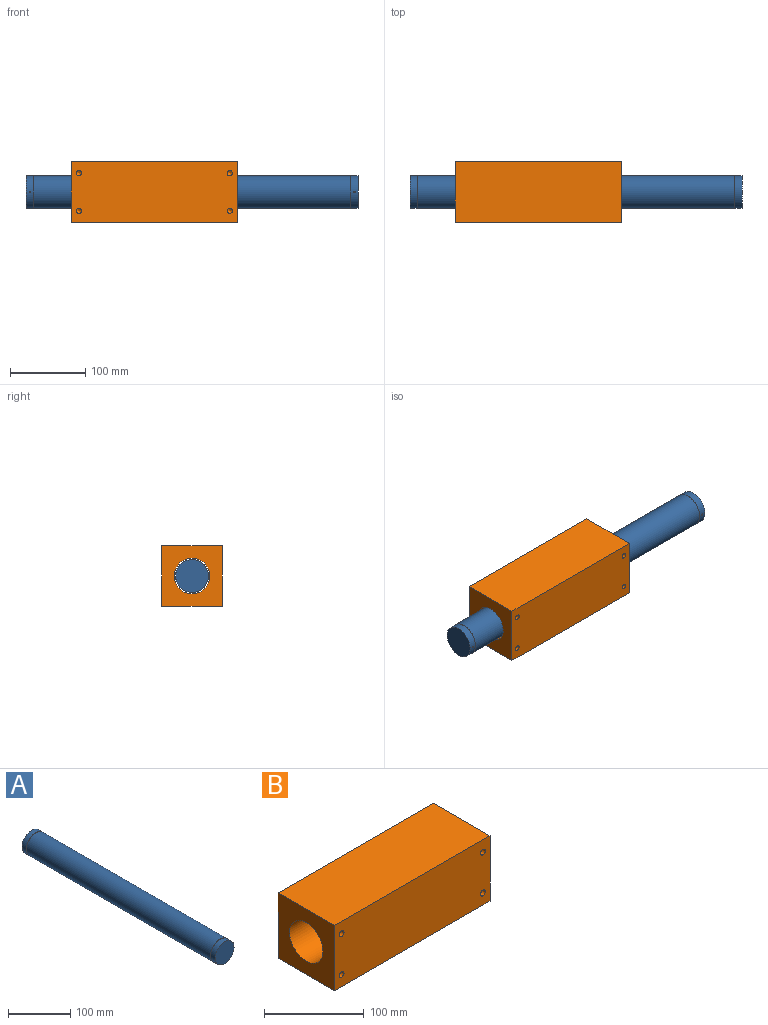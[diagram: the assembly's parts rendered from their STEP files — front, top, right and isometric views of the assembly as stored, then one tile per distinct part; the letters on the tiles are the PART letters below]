
ASSEMBLY  parts=2 mates=1
PART A: 11 faces, bbox 43.5x440x43.5 mm
  f0: cylinder r=21.65mm len=43.3mm, axis (0,1,0), area 1355.4mm2, adj f3,f4,f10
  f1: cylinder r=21.65mm len=43.3mm, axis (0,1,0), area 1355.4mm2, adj f5,f6,f8
  f2: cylinder r=21.75mm len=420mm, axis (0,1,0), area 57396.9mm2, adj f3,f5
  f3: plane 43.5x43.5mm, normal (0,1,0), area 13.6mm2, adj f0,f2
  f4: plane 43.3x43.3mm, normal (0,1,0), area 1472.5mm2, adj f0
  f5: plane 43.5x43.5mm, normal (0,-1,0), area 13.6mm2, adj f1,f2
  f6: plane 43.3x43.3mm, normal (0,-1,0), area 1472.5mm2, adj f1
  f7: plane 2.5x2.5mm, normal (0,0,-1), area 4.9mm2, adj f8
  f8: cylinder r=1.25mm len=21.65mm, axis (0,0,1), area 169.9mm2, adj f1,f7
  f9: plane 2.5x2.5mm, normal (0,0,-1), area 4.9mm2, adj f10
  f10: cylinder r=1.25mm len=21.65mm, axis (0,0,1), area 169.9mm2, adj f0,f9
PART B: 15 faces, bbox 220x80x80 mm
  f0: plane 80x80mm, normal (-1,0,0), area 4646.5mm2, adj f1,f3,f4,f5,f14
  f1: plane 220x80mm, normal (0,0,-1), area 17600mm2, adj f0,f2,f4,f5
  f2: plane 80x80mm, normal (1,0,0), area 4646.5mm2, adj f1,f3,f4,f5,f14
  f3: plane 220x80mm, normal (0,0,1), area 17600mm2, adj f0,f2,f4,f5
  f4: plane 220x80mm, normal (0,-1,0), area 17454.7mm2, adj f0,f1,f2,f3,f7,f9,f11,f13
  f5: plane 220x80mm, normal (0,1,0), area 17600mm2, adj f0,f1,f2,f3
  f6: cone r=0mm half-angle=59deg, axis (0,-1,0), area 42.4mm2, adj f7
  f7: cylinder r=3.4mm len=14.25mm, axis (0,-1,0), area 304.4mm2, adj f4,f6
  f8: cone r=0mm half-angle=59deg, axis (0,-1,0), area 42.4mm2, adj f9
  f9: cylinder r=3.4mm len=14.25mm, axis (0,-1,0), area 304.4mm2, adj f4,f8
  f10: cone r=0mm half-angle=59deg, axis (0,-1,0), area 42.4mm2, adj f11
  f11: cylinder r=3.4mm len=14.25mm, axis (0,-1,0), area 304.4mm2, adj f4,f10
  f12: cone r=0mm half-angle=59deg, axis (0,-1,0), area 42.4mm2, adj f13
  f13: cylinder r=3.4mm len=14.25mm, axis (0,-1,0), area 304.4mm2, adj f4,f12
  f14: cylinder r=23.62mm len=220mm, axis (-1,0,0), area 32656.9mm2, adj f0,f2
PLACE A rot(axis=(-0.58,-0.58,-0.58),120deg) t=(562,-40,40)mm
PLACE B t=(182,0,0)mm fixed
MATE slider A.f0 <-> B.f14  axis (-1,0,0) through (122,-40,40)mm
